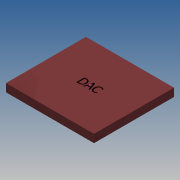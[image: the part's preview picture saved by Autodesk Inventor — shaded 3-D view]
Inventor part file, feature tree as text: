
AUTODESK INVENTOR PART (.ipt)
format: ipt  version: 2016 SP2 (Build 200236200, 236)  size: 87,552 bytes
history: native  units: mm
features: sketch x2, extrude x1
ambient origin geometry x8: Origin, YZ Plane, XZ Plane, XY Plane, X Axis, Y Axis, Z Axis, Center Point
bodies: Solid1 (feature_tree)
feature tree (3):
  extrude  "Extrusion1"  Depth=120.0mm
  sketch  "Sketch2"  dims[d2=10.0mm d3=0.0mm]
  sketch  "Sketch1"  dims[d0=65.0mm d1=120.0mm]
